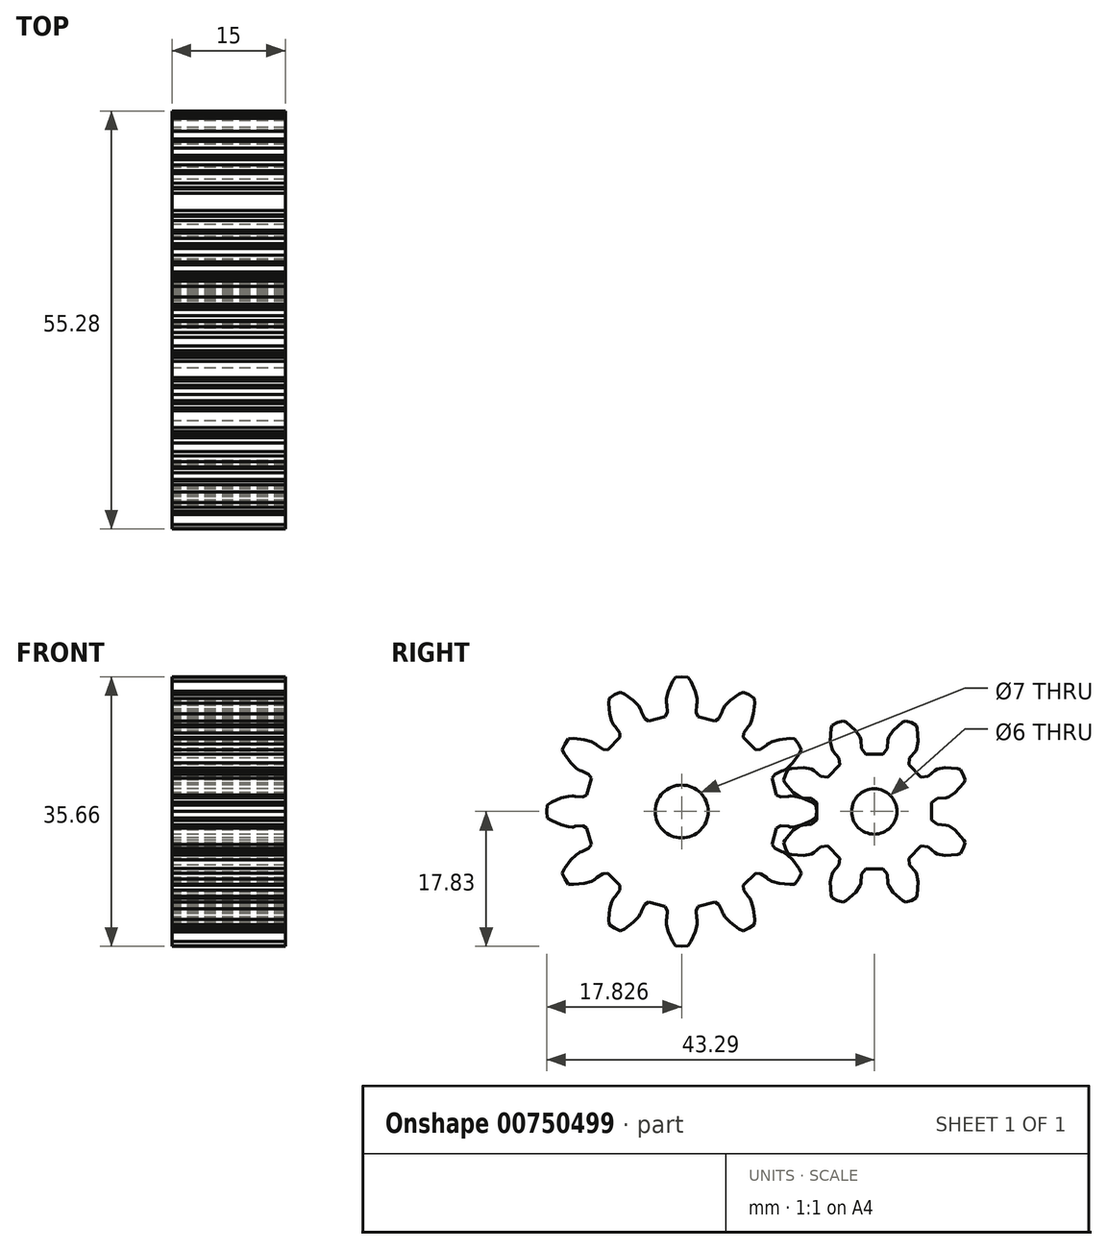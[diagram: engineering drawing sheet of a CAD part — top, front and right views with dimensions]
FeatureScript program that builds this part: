
annotation { "Feature Type Name" : "Feature", "Feature Type Description" : "" }
export const myFeature = defineFeature(function(context is Context, id is Id, definition is map)
    precondition{}
    {
        {
            var Q0;
            Q0=qCreatedBy(makeId("Right.planeOp"),FACE);
            var sketch = newSketch(context, id + "F0", { "sketchPlane" : qUnion([Q0])});
            skLineSegment(sketch, "E0", {"start": v(5.14, -9.6) * mm, "end": v(5.62, -8.91) * mm});
            skLineSegment(sketch, "E1", {"start": v(5.62, -8.91) * mm, "end": v(5.98, -8.15) * mm});
            skLineSegment(sketch, "E2", {"start": v(5.98, -8.15) * mm, "end": v(5.69, -7.55) * mm});
            skLineSegment(sketch, "E3", {"start": v(5.69, -7.55) * mm, "end": v(4.86, -6.4) * mm});
            skLineSegment(sketch, "E4", {"start": v(4.86, -6.4) * mm, "end": v(4.16, -5.74) * mm});
            skLineSegment(sketch, "E5", {"start": v(4.16, -5.74) * mm, "end": v(3.72, -5.44) * mm});
            skLineSegment(sketch, "E6", {"start": v(3.72, -5.44) * mm, "end": v(3.64, -5.4) * mm});
            skLineSegment(sketch, "E7", {"start": v(3.64, -5.4) * mm, "end": v(3.38, -5.34) * mm});
            skLineSegment(sketch, "E8", {"start": v(3.38, -5.34) * mm, "end": v(2.49, -4.9) * mm});
            skLineSegment(sketch, "E9", {"start": v(2.49, -4.9) * mm, "end": v(2.14, -4.38) * mm});
            skLineSegment(sketch, "E10", {"start": v(2.14, -4.38) * mm, "end": v(2.73, -2.18) * mm});
            skLineSegment(sketch, "E11", {"start": v(2.73, -2.18) * mm, "end": v(3.29, -1.91) * mm});
            skLineSegment(sketch, "E12", {"start": v(3.29, -1.91) * mm, "end": v(4.29, -1.97) * mm});
            skLineSegment(sketch, "E13", {"start": v(4.29, -1.97) * mm, "end": v(4.54, -2.04) * mm});
            skLineSegment(sketch, "E14", {"start": v(4.54, -2.04) * mm, "end": v(4.62, -2.05) * mm});
            skLineSegment(sketch, "E15", {"start": v(4.62, -2.05) * mm, "end": v(5.15, -2.02) * mm});
            skLineSegment(sketch, "E16", {"start": v(5.15, -2.02) * mm, "end": v(6.1, -1.79) * mm});
            skLineSegment(sketch, "E17", {"start": v(6.1, -1.79) * mm, "end": v(7.39, -1.21) * mm});
            skLineSegment(sketch, "E18", {"start": v(7.39, -1.21) * mm, "end": v(7.94, -0.84) * mm});
            skLineSegment(sketch, "E19", {"start": v(7.94, -0.84) * mm, "end": v(8.01, 0) * mm});
            skLineSegment(sketch, "E20", {"start": v(8.01, 0) * mm, "end": v(7.94, 0.84) * mm});
            skLineSegment(sketch, "E21", {"start": v(7.94, 0.84) * mm, "end": v(7.39, 1.21) * mm});
            skLineSegment(sketch, "E22", {"start": v(7.39, 1.21) * mm, "end": v(6.1, 1.79) * mm});
            skLineSegment(sketch, "E23", {"start": v(6.1, 1.79) * mm, "end": v(5.15, 2.02) * mm});
            skLineSegment(sketch, "E24", {"start": v(5.15, 2.02) * mm, "end": v(4.62, 2.05) * mm});
            skLineSegment(sketch, "E25", {"start": v(4.62, 2.05) * mm, "end": v(4.54, 2.04) * mm});
            skLineSegment(sketch, "E26", {"start": v(4.54, 2.04) * mm, "end": v(4.29, 1.97) * mm});
            skLineSegment(sketch, "E27", {"start": v(4.29, 1.97) * mm, "end": v(3.29, 1.91) * mm});
            skLineSegment(sketch, "E28", {"start": v(3.29, 1.91) * mm, "end": v(2.73, 2.18) * mm});
            skLineSegment(sketch, "E29", {"start": v(2.73, 2.18) * mm, "end": v(2.14, 4.38) * mm});
            skLineSegment(sketch, "E30", {"start": v(2.14, 4.38) * mm, "end": v(2.49, 4.9) * mm});
            skLineSegment(sketch, "E31", {"start": v(2.49, 4.9) * mm, "end": v(3.38, 5.34) * mm});
            skLineSegment(sketch, "E32", {"start": v(3.38, 5.34) * mm, "end": v(3.64, 5.4) * mm});
            skLineSegment(sketch, "E33", {"start": v(3.64, 5.4) * mm, "end": v(3.72, 5.44) * mm});
            skLineSegment(sketch, "E34", {"start": v(3.72, 5.44) * mm, "end": v(4.16, 5.74) * mm});
            skLineSegment(sketch, "E35", {"start": v(4.16, 5.74) * mm, "end": v(4.86, 6.4) * mm});
            skLineSegment(sketch, "E36", {"start": v(4.86, 6.4) * mm, "end": v(5.69, 7.55) * mm});
            skLineSegment(sketch, "E37", {"start": v(5.69, 7.55) * mm, "end": v(5.98, 8.15) * mm});
            skLineSegment(sketch, "E38", {"start": v(5.98, 8.15) * mm, "end": v(5.62, 8.91) * mm});
            skLineSegment(sketch, "E39", {"start": v(5.62, 8.91) * mm, "end": v(5.14, 9.6) * mm});
            skLineSegment(sketch, "E40", {"start": v(5.14, 9.6) * mm, "end": v(4.48, 9.65) * mm});
            skLineSegment(sketch, "E41", {"start": v(4.48, 9.65) * mm, "end": v(3.07, 9.5) * mm});
            skLineSegment(sketch, "E42", {"start": v(3.07, 9.5) * mm, "end": v(2.14, 9.23) * mm});
            skLineSegment(sketch, "E43", {"start": v(2.14, 9.23) * mm, "end": v(1.66, 9) * mm});
            skLineSegment(sketch, "E44", {"start": v(1.66, 9) * mm, "end": v(1.6, 8.95) * mm});
            skLineSegment(sketch, "E45", {"start": v(1.6, 8.95) * mm, "end": v(1.41, 8.76) * mm});
            skLineSegment(sketch, "E46", {"start": v(1.41, 8.76) * mm, "end": v(0.58, 8.2) * mm});
            skLineSegment(sketch, "E47", {"start": v(0.58, 8.2) * mm, "end": v(-0.04, 8.16) * mm});
            skLineSegment(sketch, "E48", {"start": v(-0.04, 8.16) * mm, "end": v(-1.65, 9.77) * mm});
            skLineSegment(sketch, "E49", {"start": v(-1.65, 9.77) * mm, "end": v(-1.6, 10.4) * mm});
            skLineSegment(sketch, "E50", {"start": v(-1.6, 10.4) * mm, "end": v(-1.06, 11.23) * mm});
            skLineSegment(sketch, "E51", {"start": v(-1.06, 11.23) * mm, "end": v(-0.87, 11.4) * mm});
            skLineSegment(sketch, "E52", {"start": v(-0.87, 11.4) * mm, "end": v(-0.82, 11.48) * mm});
            skLineSegment(sketch, "E53", {"start": v(-0.82, 11.48) * mm, "end": v(-0.58, 11.95) * mm});
            skLineSegment(sketch, "E54", {"start": v(-0.58, 11.95) * mm, "end": v(-0.31, 12.88) * mm});
            skLineSegment(sketch, "E55", {"start": v(-0.31, 12.88) * mm, "end": v(-0.16, 14.29) * mm});
            skLineSegment(sketch, "E56", {"start": v(-0.16, 14.29) * mm, "end": v(-0.2, 14.95) * mm});
            skLineSegment(sketch, "E57", {"start": v(-0.2, 14.95) * mm, "end": v(-0.9, 15.44) * mm});
            skLineSegment(sketch, "E58", {"start": v(-0.9, 15.44) * mm, "end": v(-1.67, 15.8) * mm});
            skLineSegment(sketch, "E59", {"start": v(-1.67, 15.8) * mm, "end": v(-2.26, 15.5) * mm});
            skLineSegment(sketch, "E60", {"start": v(-2.26, 15.5) * mm, "end": v(-3.4, 14.67) * mm});
            skLineSegment(sketch, "E61", {"start": v(-3.4, 14.67) * mm, "end": v(-4.08, 13.97) * mm});
            skLineSegment(sketch, "E62", {"start": v(-4.08, 13.97) * mm, "end": v(-4.37, 13.53) * mm});
            skLineSegment(sketch, "E63", {"start": v(-4.37, 13.53) * mm, "end": v(-4.41, 13.45) * mm});
            skLineSegment(sketch, "E64", {"start": v(-4.41, 13.45) * mm, "end": v(-4.47, 13.2) * mm});
            skLineSegment(sketch, "E65", {"start": v(-4.47, 13.2) * mm, "end": v(-4.92, 12.3) * mm});
            skLineSegment(sketch, "E66", {"start": v(-4.92, 12.3) * mm, "end": v(-5.43, 11.96) * mm});
            skLineSegment(sketch, "E67", {"start": v(-5.43, 11.96) * mm, "end": v(-7.63, 12.54) * mm});
            skLineSegment(sketch, "E68", {"start": v(-7.63, 12.54) * mm, "end": v(-7.9, 13.1) * mm});
            skLineSegment(sketch, "E69", {"start": v(-7.9, 13.1) * mm, "end": v(-7.84, 14.1) * mm});
            skLineSegment(sketch, "E70", {"start": v(-7.84, 14.1) * mm, "end": v(-7.77, 14.35) * mm});
            skLineSegment(sketch, "E71", {"start": v(-7.77, 14.35) * mm, "end": v(-7.76, 14.44) * mm});
            skLineSegment(sketch, "E72", {"start": v(-7.76, 14.44) * mm, "end": v(-7.8, 14.97) * mm});
            skLineSegment(sketch, "E73", {"start": v(-7.8, 14.97) * mm, "end": v(-8.03, 15.9) * mm});
            skLineSegment(sketch, "E74", {"start": v(-8.03, 15.9) * mm, "end": v(-8.6, 17.2) * mm});
            skLineSegment(sketch, "E75", {"start": v(-8.6, 17.2) * mm, "end": v(-8.97, 17.75) * mm});
            skLineSegment(sketch, "E76", {"start": v(-8.97, 17.75) * mm, "end": v(-9.81, 17.83) * mm});
            skLineSegment(sketch, "E77", {"start": v(-9.81, 17.83) * mm, "end": v(-10.66, 17.75) * mm});
            skLineSegment(sketch, "E78", {"start": v(-10.66, 17.75) * mm, "end": v(-11.03, 17.2) * mm});
            skLineSegment(sketch, "E79", {"start": v(-11.03, 17.2) * mm, "end": v(-11.6, 15.9) * mm});
            skLineSegment(sketch, "E80", {"start": v(-11.6, 15.9) * mm, "end": v(-11.83, 14.97) * mm});
            skLineSegment(sketch, "E81", {"start": v(-11.83, 14.97) * mm, "end": v(-11.87, 14.44) * mm});
            skLineSegment(sketch, "E82", {"start": v(-11.87, 14.44) * mm, "end": v(-11.86, 14.35) * mm});
            skLineSegment(sketch, "E83", {"start": v(-11.86, 14.35) * mm, "end": v(-11.79, 14.1) * mm});
            skLineSegment(sketch, "E84", {"start": v(-11.79, 14.1) * mm, "end": v(-11.73, 13.1) * mm});
            skLineSegment(sketch, "E85", {"start": v(-11.73, 13.1) * mm, "end": v(-12, 12.54) * mm});
            skLineSegment(sketch, "E86", {"start": v(-12, 12.54) * mm, "end": v(-14.2, 11.96) * mm});
            skLineSegment(sketch, "E87", {"start": v(-14.2, 11.96) * mm, "end": v(-14.71, 12.3) * mm});
            skLineSegment(sketch, "E88", {"start": v(-14.71, 12.3) * mm, "end": v(-15.16, 13.2) * mm});
            skLineSegment(sketch, "E89", {"start": v(-15.16, 13.2) * mm, "end": v(-15.22, 13.45) * mm});
            skLineSegment(sketch, "E90", {"start": v(-15.22, 13.45) * mm, "end": v(-15.25, 13.53) * mm});
            skLineSegment(sketch, "E91", {"start": v(-15.25, 13.53) * mm, "end": v(-15.55, 13.97) * mm});
            skLineSegment(sketch, "E92", {"start": v(-15.55, 13.97) * mm, "end": v(-16.22, 14.67) * mm});
            skLineSegment(sketch, "E93", {"start": v(-16.22, 14.67) * mm, "end": v(-17.36, 15.5) * mm});
            skLineSegment(sketch, "E94", {"start": v(-17.36, 15.5) * mm, "end": v(-17.96, 15.8) * mm});
            skLineSegment(sketch, "E95", {"start": v(-17.96, 15.8) * mm, "end": v(-18.73, 15.44) * mm});
            skLineSegment(sketch, "E96", {"start": v(-18.73, 15.44) * mm, "end": v(-19.42, 14.95) * mm});
            skLineSegment(sketch, "E97", {"start": v(-19.42, 14.95) * mm, "end": v(-19.47, 14.29) * mm});
            skLineSegment(sketch, "E98", {"start": v(-19.47, 14.29) * mm, "end": v(-19.32, 12.88) * mm});
            skLineSegment(sketch, "E99", {"start": v(-19.32, 12.88) * mm, "end": v(-19.05, 11.95) * mm});
            skLineSegment(sketch, "E100", {"start": v(-19.05, 11.95) * mm, "end": v(-18.81, 11.48) * mm});
            skLineSegment(sketch, "E101", {"start": v(-18.81, 11.48) * mm, "end": v(-18.76, 11.4) * mm});
            skLineSegment(sketch, "E102", {"start": v(-18.76, 11.4) * mm, "end": v(-18.57, 11.23) * mm});
            skLineSegment(sketch, "E103", {"start": v(-18.57, 11.23) * mm, "end": v(-18.02, 10.4) * mm});
            skLineSegment(sketch, "E104", {"start": v(-18.02, 10.4) * mm, "end": v(-17.98, 9.77) * mm});
            skLineSegment(sketch, "E105", {"start": v(-17.98, 9.77) * mm, "end": v(-19.59, 8.16) * mm});
            skLineSegment(sketch, "E106", {"start": v(-19.59, 8.16) * mm, "end": v(-20.2, 8.2) * mm});
            skLineSegment(sketch, "E107", {"start": v(-20.2, 8.2) * mm, "end": v(-21.04, 8.76) * mm});
            skLineSegment(sketch, "E108", {"start": v(-21.04, 8.76) * mm, "end": v(-21.22, 8.95) * mm});
            skLineSegment(sketch, "E109", {"start": v(-21.22, 8.95) * mm, "end": v(-21.3, 9) * mm});
            skLineSegment(sketch, "E110", {"start": v(-21.3, 9) * mm, "end": v(-21.77, 9.23) * mm});
            skLineSegment(sketch, "E111", {"start": v(-21.77, 9.23) * mm, "end": v(-22.7, 9.5) * mm});
            skLineSegment(sketch, "E112", {"start": v(-22.7, 9.5) * mm, "end": v(-24.1, 9.65) * mm});
            skLineSegment(sketch, "E113", {"start": v(-24.1, 9.65) * mm, "end": v(-24.77, 9.6) * mm});
            skLineSegment(sketch, "E114", {"start": v(-24.77, 9.6) * mm, "end": v(-25.25, 8.91) * mm});
            skLineSegment(sketch, "E115", {"start": v(-25.25, 8.91) * mm, "end": v(-25.6, 8.15) * mm});
            skLineSegment(sketch, "E116", {"start": v(-25.6, 8.15) * mm, "end": v(-25.32, 7.55) * mm});
            skLineSegment(sketch, "E117", {"start": v(-25.32, 7.55) * mm, "end": v(-24.48, 6.4) * mm});
            skLineSegment(sketch, "E118", {"start": v(-24.48, 6.4) * mm, "end": v(-23.78, 5.74) * mm});
            skLineSegment(sketch, "E119", {"start": v(-23.78, 5.74) * mm, "end": v(-23.34, 5.44) * mm});
            skLineSegment(sketch, "E120", {"start": v(-23.34, 5.44) * mm, "end": v(-23.26, 5.4) * mm});
            skLineSegment(sketch, "E121", {"start": v(-23.26, 5.4) * mm, "end": v(-23.01, 5.34) * mm});
            skLineSegment(sketch, "E122", {"start": v(-23.01, 5.34) * mm, "end": v(-22.12, 4.9) * mm});
            skLineSegment(sketch, "E123", {"start": v(-22.12, 4.9) * mm, "end": v(-21.77, 4.38) * mm});
            skLineSegment(sketch, "E124", {"start": v(-21.77, 4.38) * mm, "end": v(-22.36, 2.18) * mm});
            skLineSegment(sketch, "E125", {"start": v(-22.36, 2.18) * mm, "end": v(-22.92, 1.91) * mm});
            skLineSegment(sketch, "E126", {"start": v(-22.92, 1.91) * mm, "end": v(-23.92, 1.97) * mm});
            skLineSegment(sketch, "E127", {"start": v(-23.92, 1.97) * mm, "end": v(-24.16, 2.04) * mm});
            skLineSegment(sketch, "E128", {"start": v(-24.16, 2.04) * mm, "end": v(-24.25, 2.05) * mm});
            skLineSegment(sketch, "E129", {"start": v(-24.25, 2.05) * mm, "end": v(-24.78, 2.02) * mm});
            skLineSegment(sketch, "E130", {"start": v(-24.78, 2.02) * mm, "end": v(-25.72, 1.79) * mm});
            skLineSegment(sketch, "E131", {"start": v(-25.72, 1.79) * mm, "end": v(-27.02, 1.21) * mm});
            skLineSegment(sketch, "E132", {"start": v(-27.02, 1.21) * mm, "end": v(-27.57, 0.84) * mm});
            skLineSegment(sketch, "E133", {"start": v(-27.57, 0.84) * mm, "end": v(-27.64, 0) * mm});
            skLineSegment(sketch, "E134", {"start": v(-27.64, 0) * mm, "end": v(-27.57, -0.84) * mm});
            skLineSegment(sketch, "E135", {"start": v(-27.57, -0.84) * mm, "end": v(-27.02, -1.21) * mm});
            skLineSegment(sketch, "E136", {"start": v(-27.02, -1.21) * mm, "end": v(-25.72, -1.79) * mm});
            skLineSegment(sketch, "E137", {"start": v(-25.72, -1.79) * mm, "end": v(-24.78, -2.02) * mm});
            skLineSegment(sketch, "E138", {"start": v(-24.78, -2.02) * mm, "end": v(-24.25, -2.05) * mm});
            skLineSegment(sketch, "E139", {"start": v(-24.25, -2.05) * mm, "end": v(-24.16, -2.04) * mm});
            skLineSegment(sketch, "E140", {"start": v(-24.16, -2.04) * mm, "end": v(-23.92, -1.97) * mm});
            skLineSegment(sketch, "E141", {"start": v(-23.92, -1.97) * mm, "end": v(-22.92, -1.91) * mm});
            skLineSegment(sketch, "E142", {"start": v(-22.92, -1.91) * mm, "end": v(-22.36, -2.18) * mm});
            skLineSegment(sketch, "E143", {"start": v(-22.36, -2.18) * mm, "end": v(-21.77, -4.38) * mm});
            skLineSegment(sketch, "E144", {"start": v(-21.77, -4.38) * mm, "end": v(-22.12, -4.9) * mm});
            skLineSegment(sketch, "E145", {"start": v(-22.12, -4.9) * mm, "end": v(-23.01, -5.34) * mm});
            skLineSegment(sketch, "E146", {"start": v(-23.01, -5.34) * mm, "end": v(-23.26, -5.4) * mm});
            skLineSegment(sketch, "E147", {"start": v(-23.26, -5.4) * mm, "end": v(-23.34, -5.44) * mm});
            skLineSegment(sketch, "E148", {"start": v(-23.34, -5.44) * mm, "end": v(-23.78, -5.74) * mm});
            skLineSegment(sketch, "E149", {"start": v(-23.78, -5.74) * mm, "end": v(-24.48, -6.4) * mm});
            skLineSegment(sketch, "E150", {"start": v(-24.48, -6.4) * mm, "end": v(-25.32, -7.55) * mm});
            skLineSegment(sketch, "E151", {"start": v(-25.32, -7.55) * mm, "end": v(-25.6, -8.15) * mm});
            skLineSegment(sketch, "E152", {"start": v(-25.6, -8.15) * mm, "end": v(-25.25, -8.91) * mm});
            skLineSegment(sketch, "E153", {"start": v(-25.25, -8.91) * mm, "end": v(-24.77, -9.6) * mm});
            skLineSegment(sketch, "E154", {"start": v(-24.77, -9.6) * mm, "end": v(-24.1, -9.65) * mm});
            skLineSegment(sketch, "E155", {"start": v(-24.1, -9.65) * mm, "end": v(-22.7, -9.5) * mm});
            skLineSegment(sketch, "E156", {"start": v(-22.7, -9.5) * mm, "end": v(-21.77, -9.23) * mm});
            skLineSegment(sketch, "E157", {"start": v(-21.77, -9.23) * mm, "end": v(-21.3, -9) * mm});
            skLineSegment(sketch, "E158", {"start": v(-21.3, -9) * mm, "end": v(-21.22, -8.95) * mm});
            skLineSegment(sketch, "E159", {"start": v(-21.22, -8.95) * mm, "end": v(-21.04, -8.76) * mm});
            skLineSegment(sketch, "E160", {"start": v(-21.04, -8.76) * mm, "end": v(-20.2, -8.2) * mm});
            skLineSegment(sketch, "E161", {"start": v(-20.2, -8.2) * mm, "end": v(-19.59, -8.16) * mm});
            skLineSegment(sketch, "E162", {"start": v(-19.59, -8.16) * mm, "end": v(-17.98, -9.77) * mm});
            skLineSegment(sketch, "E163", {"start": v(-17.98, -9.77) * mm, "end": v(-18.02, -10.4) * mm});
            skLineSegment(sketch, "E164", {"start": v(-18.02, -10.4) * mm, "end": v(-18.57, -11.23) * mm});
            skLineSegment(sketch, "E165", {"start": v(-18.57, -11.23) * mm, "end": v(-18.76, -11.4) * mm});
            skLineSegment(sketch, "E166", {"start": v(-18.76, -11.4) * mm, "end": v(-18.81, -11.48) * mm});
            skLineSegment(sketch, "E167", {"start": v(-18.81, -11.48) * mm, "end": v(-19.05, -11.95) * mm});
            skLineSegment(sketch, "E168", {"start": v(-19.05, -11.95) * mm, "end": v(-19.32, -12.88) * mm});
            skLineSegment(sketch, "E169", {"start": v(-19.32, -12.88) * mm, "end": v(-19.47, -14.29) * mm});
            skLineSegment(sketch, "E170", {"start": v(-19.47, -14.29) * mm, "end": v(-19.42, -14.95) * mm});
            skLineSegment(sketch, "E171", {"start": v(-19.42, -14.95) * mm, "end": v(-18.73, -15.44) * mm});
            skLineSegment(sketch, "E172", {"start": v(-18.73, -15.44) * mm, "end": v(-17.96, -15.8) * mm});
            skLineSegment(sketch, "E173", {"start": v(-17.96, -15.8) * mm, "end": v(-17.36, -15.5) * mm});
            skLineSegment(sketch, "E174", {"start": v(-17.36, -15.5) * mm, "end": v(-16.22, -14.67) * mm});
            skLineSegment(sketch, "E175", {"start": v(-16.22, -14.67) * mm, "end": v(-15.55, -13.97) * mm});
            skLineSegment(sketch, "E176", {"start": v(-15.55, -13.97) * mm, "end": v(-15.25, -13.53) * mm});
            skLineSegment(sketch, "E177", {"start": v(-15.25, -13.53) * mm, "end": v(-15.22, -13.45) * mm});
            skLineSegment(sketch, "E178", {"start": v(-15.22, -13.45) * mm, "end": v(-15.16, -13.2) * mm});
            skLineSegment(sketch, "E179", {"start": v(-15.16, -13.2) * mm, "end": v(-14.71, -12.3) * mm});
            skLineSegment(sketch, "E180", {"start": v(-14.71, -12.3) * mm, "end": v(-14.2, -11.96) * mm});
            skLineSegment(sketch, "E181", {"start": v(-14.2, -11.96) * mm, "end": v(-12, -12.54) * mm});
            skLineSegment(sketch, "E182", {"start": v(-12, -12.54) * mm, "end": v(-11.73, -13.1) * mm});
            skLineSegment(sketch, "E183", {"start": v(-11.73, -13.1) * mm, "end": v(-11.79, -14.1) * mm});
            skLineSegment(sketch, "E184", {"start": v(-11.79, -14.1) * mm, "end": v(-11.86, -14.35) * mm});
            skLineSegment(sketch, "E185", {"start": v(-11.86, -14.35) * mm, "end": v(-11.87, -14.44) * mm});
            skLineSegment(sketch, "E186", {"start": v(-11.87, -14.44) * mm, "end": v(-11.83, -14.97) * mm});
            skLineSegment(sketch, "E187", {"start": v(-11.83, -14.97) * mm, "end": v(-11.6, -15.9) * mm});
            skLineSegment(sketch, "E188", {"start": v(-11.6, -15.9) * mm, "end": v(-11.03, -17.2) * mm});
            skLineSegment(sketch, "E189", {"start": v(-11.03, -17.2) * mm, "end": v(-10.66, -17.75) * mm});
            skLineSegment(sketch, "E190", {"start": v(-10.66, -17.75) * mm, "end": v(-9.81, -17.83) * mm});
            skLineSegment(sketch, "E191", {"start": v(-9.81, -17.83) * mm, "end": v(-8.97, -17.75) * mm});
            skLineSegment(sketch, "E192", {"start": v(-8.97, -17.75) * mm, "end": v(-8.6, -17.2) * mm});
            skLineSegment(sketch, "E193", {"start": v(-8.6, -17.2) * mm, "end": v(-8.03, -15.9) * mm});
            skLineSegment(sketch, "E194", {"start": v(-8.03, -15.9) * mm, "end": v(-7.8, -14.97) * mm});
            skLineSegment(sketch, "E195", {"start": v(-7.8, -14.97) * mm, "end": v(-7.76, -14.44) * mm});
            skLineSegment(sketch, "E196", {"start": v(-7.76, -14.44) * mm, "end": v(-7.77, -14.35) * mm});
            skLineSegment(sketch, "E197", {"start": v(-7.77, -14.35) * mm, "end": v(-7.84, -14.1) * mm});
            skLineSegment(sketch, "E198", {"start": v(-7.84, -14.1) * mm, "end": v(-7.9, -13.1) * mm});
            skLineSegment(sketch, "E199", {"start": v(-7.9, -13.1) * mm, "end": v(-7.63, -12.54) * mm});
            skLineSegment(sketch, "E200", {"start": v(-7.63, -12.54) * mm, "end": v(-5.43, -11.96) * mm});
            skLineSegment(sketch, "E201", {"start": v(-5.43, -11.96) * mm, "end": v(-4.92, -12.3) * mm});
            skLineSegment(sketch, "E202", {"start": v(-4.92, -12.3) * mm, "end": v(-4.47, -13.2) * mm});
            skLineSegment(sketch, "E203", {"start": v(-4.47, -13.2) * mm, "end": v(-4.41, -13.45) * mm});
            skLineSegment(sketch, "E204", {"start": v(-4.41, -13.45) * mm, "end": v(-4.37, -13.53) * mm});
            skLineSegment(sketch, "E205", {"start": v(-4.37, -13.53) * mm, "end": v(-4.08, -13.97) * mm});
            skLineSegment(sketch, "E206", {"start": v(-4.08, -13.97) * mm, "end": v(-3.4, -14.67) * mm});
            skLineSegment(sketch, "E207", {"start": v(-3.4, -14.67) * mm, "end": v(-2.26, -15.5) * mm});
            skLineSegment(sketch, "E208", {"start": v(-2.26, -15.5) * mm, "end": v(-1.67, -15.8) * mm});
            skLineSegment(sketch, "E209", {"start": v(-1.67, -15.8) * mm, "end": v(-0.9, -15.44) * mm});
            skLineSegment(sketch, "E210", {"start": v(-0.9, -15.44) * mm, "end": v(-0.2, -14.95) * mm});
            skLineSegment(sketch, "E211", {"start": v(-0.2, -14.95) * mm, "end": v(-0.16, -14.29) * mm});
            skLineSegment(sketch, "E212", {"start": v(-0.16, -14.29) * mm, "end": v(-0.31, -12.88) * mm});
            skLineSegment(sketch, "E213", {"start": v(-0.31, -12.88) * mm, "end": v(-0.58, -11.95) * mm});
            skLineSegment(sketch, "E214", {"start": v(-0.58, -11.95) * mm, "end": v(-0.82, -11.48) * mm});
            skLineSegment(sketch, "E215", {"start": v(-0.82, -11.48) * mm, "end": v(-0.87, -11.4) * mm});
            skLineSegment(sketch, "E216", {"start": v(-0.87, -11.4) * mm, "end": v(-1.06, -11.23) * mm});
            skLineSegment(sketch, "E217", {"start": v(-1.06, -11.23) * mm, "end": v(-1.6, -10.4) * mm});
            skLineSegment(sketch, "E218", {"start": v(-1.6, -10.4) * mm, "end": v(-1.65, -9.77) * mm});
            skLineSegment(sketch, "E219", {"start": v(-1.65, -9.77) * mm, "end": v(-0.04, -8.16) * mm});
            skLineSegment(sketch, "E220", {"start": v(-0.04, -8.16) * mm, "end": v(0.58, -8.2) * mm});
            skLineSegment(sketch, "E221", {"start": v(0.58, -8.2) * mm, "end": v(1.41, -8.76) * mm});
            skLineSegment(sketch, "E222", {"start": v(1.41, -8.76) * mm, "end": v(1.6, -8.95) * mm});
            skLineSegment(sketch, "E223", {"start": v(1.6, -8.95) * mm, "end": v(1.66, -9) * mm});
            skLineSegment(sketch, "E224", {"start": v(1.66, -9) * mm, "end": v(2.14, -9.23) * mm});
            skLineSegment(sketch, "E225", {"start": v(2.14, -9.23) * mm, "end": v(3.07, -9.5) * mm});
            skLineSegment(sketch, "E226", {"start": v(3.07, -9.5) * mm, "end": v(4.48, -9.65) * mm});
            skLineSegment(sketch, "E227", {"start": v(4.48, -9.65) * mm, "end": v(5.14, -9.6) * mm});
            skLineSegment(sketch, "E228", {"start": v(-9.4, -1.96) * mm, "end": v(-9.81, -2) * mm});
            skLineSegment(sketch, "E229", {"start": v(-9.81, -2) * mm, "end": v(-10.23, -1.96) * mm});
            skLineSegment(sketch, "E230", {"start": v(-10.23, -1.96) * mm, "end": v(-10.63, -1.83) * mm});
            skLineSegment(sketch, "E231", {"start": v(-10.63, -1.83) * mm, "end": v(-10.99, -1.62) * mm});
            skLineSegment(sketch, "E232", {"start": v(-10.99, -1.62) * mm, "end": v(-11.3, -1.34) * mm});
            skLineSegment(sketch, "E233", {"start": v(-11.3, -1.34) * mm, "end": v(-11.55, -1) * mm});
            skLineSegment(sketch, "E234", {"start": v(-11.55, -1) * mm, "end": v(-11.72, -0.62) * mm});
            skLineSegment(sketch, "E235", {"start": v(-11.72, -0.62) * mm, "end": v(-11.8, -0.2) * mm});
            skLineSegment(sketch, "E236", {"start": v(-11.8, -0.2) * mm, "end": v(-11.8, 0.2) * mm});
            skLineSegment(sketch, "E237", {"start": v(-11.8, 0.2) * mm, "end": v(-11.72, 0.62) * mm});
            skLineSegment(sketch, "E238", {"start": v(-11.72, 0.62) * mm, "end": v(-11.55, 1) * mm});
            skLineSegment(sketch, "E239", {"start": v(-11.55, 1) * mm, "end": v(-11.3, 1.34) * mm});
            skLineSegment(sketch, "E240", {"start": v(-11.3, 1.34) * mm, "end": v(-10.99, 1.62) * mm});
            skLineSegment(sketch, "E241", {"start": v(-10.99, 1.62) * mm, "end": v(-10.63, 1.83) * mm});
            skLineSegment(sketch, "E242", {"start": v(-10.63, 1.83) * mm, "end": v(-10.23, 1.96) * mm});
            skLineSegment(sketch, "E243", {"start": v(-10.23, 1.96) * mm, "end": v(-9.81, 2) * mm});
            skLineSegment(sketch, "E244", {"start": v(-9.81, 2) * mm, "end": v(-9.4, 1.96) * mm});
            skLineSegment(sketch, "E245", {"start": v(-9.4, 1.96) * mm, "end": v(-9, 1.83) * mm});
            skLineSegment(sketch, "E246", {"start": v(-9, 1.83) * mm, "end": v(-8.64, 1.62) * mm});
            skLineSegment(sketch, "E247", {"start": v(-8.64, 1.62) * mm, "end": v(-8.33, 1.34) * mm});
            skLineSegment(sketch, "E248", {"start": v(-8.33, 1.34) * mm, "end": v(-8.08, 1) * mm});
            skLineSegment(sketch, "E249", {"start": v(-8.08, 1) * mm, "end": v(-7.91, 0.62) * mm});
            skLineSegment(sketch, "E250", {"start": v(-7.91, 0.62) * mm, "end": v(-7.83, 0.2) * mm});
            skLineSegment(sketch, "E251", {"start": v(-7.83, 0.2) * mm, "end": v(-7.83, -0.2) * mm});
            skLineSegment(sketch, "E252", {"start": v(-7.83, -0.2) * mm, "end": v(-7.91, -0.62) * mm});
            skLineSegment(sketch, "E253", {"start": v(-7.91, -0.62) * mm, "end": v(-8.08, -1) * mm});
            skLineSegment(sketch, "E254", {"start": v(-8.08, -1) * mm, "end": v(-8.33, -1.34) * mm});
            skLineSegment(sketch, "E255", {"start": v(-8.33, -1.34) * mm, "end": v(-8.64, -1.62) * mm});
            skLineSegment(sketch, "E256", {"start": v(-8.64, -1.62) * mm, "end": v(-9, -1.83) * mm});
            skLineSegment(sketch, "E257", {"start": v(-9, -1.83) * mm, "end": v(-9.4, -1.96) * mm});
            skLineSegment(sketch, "E258", {"start": v(4.25, 5.56) * mm, "end": v(3.89, 4.87) * mm});
            skLineSegment(sketch, "E259", {"start": v(3.89, 4.87) * mm, "end": v(3.66, 4.13) * mm});
            skLineSegment(sketch, "E260", {"start": v(3.66, 4.13) * mm, "end": v(3.84, 3.76) * mm});
            skLineSegment(sketch, "E261", {"start": v(3.84, 3.76) * mm, "end": v(4.96, 2.48) * mm});
            skLineSegment(sketch, "E262", {"start": v(4.96, 2.48) * mm, "end": v(5.8, 1.9) * mm});
            skLineSegment(sketch, "E263", {"start": v(5.8, 1.9) * mm, "end": v(6.15, 1.8) * mm});
            skLineSegment(sketch, "E264", {"start": v(6.15, 1.8) * mm, "end": v(7.33, 1.71) * mm});
            skLineSegment(sketch, "E265", {"start": v(7.33, 1.71) * mm, "end": v(8.06, 1.14) * mm});
            skLineSegment(sketch, "E266", {"start": v(8.06, 1.14) * mm, "end": v(8.06, -1.14) * mm});
            skLineSegment(sketch, "E267", {"start": v(8.06, -1.14) * mm, "end": v(7.33, -1.71) * mm});
            skLineSegment(sketch, "E268", {"start": v(7.33, -1.71) * mm, "end": v(6.15, -1.8) * mm});
            skLineSegment(sketch, "E269", {"start": v(6.15, -1.8) * mm, "end": v(5.8, -1.9) * mm});
            skLineSegment(sketch, "E270", {"start": v(5.8, -1.9) * mm, "end": v(4.96, -2.48) * mm});
            skLineSegment(sketch, "E271", {"start": v(4.96, -2.48) * mm, "end": v(3.84, -3.76) * mm});
            skLineSegment(sketch, "E272", {"start": v(3.84, -3.76) * mm, "end": v(3.66, -4.13) * mm});
            skLineSegment(sketch, "E273", {"start": v(3.66, -4.13) * mm, "end": v(3.89, -4.87) * mm});
            skLineSegment(sketch, "E274", {"start": v(3.89, -4.87) * mm, "end": v(4.25, -5.56) * mm});
            skLineSegment(sketch, "E275", {"start": v(4.25, -5.56) * mm, "end": v(4.65, -5.7) * mm});
            skLineSegment(sketch, "E276", {"start": v(4.65, -5.7) * mm, "end": v(6.33, -5.8) * mm});
            skLineSegment(sketch, "E277", {"start": v(6.33, -5.8) * mm, "end": v(7.34, -5.6) * mm});
            skLineSegment(sketch, "E278", {"start": v(7.34, -5.6) * mm, "end": v(7.67, -5.45) * mm});
            skLineSegment(sketch, "E279", {"start": v(7.67, -5.45) * mm, "end": v(8.56, -4.67) * mm});
            skLineSegment(sketch, "E280", {"start": v(8.56, -4.67) * mm, "end": v(9.48, -4.56) * mm});
            skLineSegment(sketch, "E281", {"start": v(9.48, -4.56) * mm, "end": v(11.09, -6.17) * mm});
            skLineSegment(sketch, "E282", {"start": v(11.09, -6.17) * mm, "end": v(10.98, -7.1) * mm});
            skLineSegment(sketch, "E283", {"start": v(10.98, -7.1) * mm, "end": v(10.2, -7.98) * mm});
            skLineSegment(sketch, "E284", {"start": v(10.2, -7.98) * mm, "end": v(10.04, -8.3) * mm});
            skLineSegment(sketch, "E285", {"start": v(10.04, -8.3) * mm, "end": v(9.84, -9.32) * mm});
            skLineSegment(sketch, "E286", {"start": v(9.84, -9.32) * mm, "end": v(9.96, -11) * mm});
            skLineSegment(sketch, "E287", {"start": v(9.96, -11) * mm, "end": v(10.1, -11.4) * mm});
            skLineSegment(sketch, "E288", {"start": v(10.1, -11.4) * mm, "end": v(10.78, -11.76) * mm});
            skLineSegment(sketch, "E289", {"start": v(10.78, -11.76) * mm, "end": v(11.52, -11.99) * mm});
            skLineSegment(sketch, "E290", {"start": v(11.52, -11.99) * mm, "end": v(11.9, -11.8) * mm});
            skLineSegment(sketch, "E291", {"start": v(11.9, -11.8) * mm, "end": v(13.17, -10.7) * mm});
            skLineSegment(sketch, "E292", {"start": v(13.17, -10.7) * mm, "end": v(13.74, -9.84) * mm});
            skLineSegment(sketch, "E293", {"start": v(13.74, -9.84) * mm, "end": v(13.86, -9.5) * mm});
            skLineSegment(sketch, "E294", {"start": v(13.86, -9.5) * mm, "end": v(13.94, -8.32) * mm});
            skLineSegment(sketch, "E295", {"start": v(13.94, -8.32) * mm, "end": v(14.51, -7.59) * mm});
            skLineSegment(sketch, "E296", {"start": v(14.51, -7.59) * mm, "end": v(16.79, -7.59) * mm});
            skLineSegment(sketch, "E297", {"start": v(16.79, -7.59) * mm, "end": v(17.36, -8.32) * mm});
            skLineSegment(sketch, "E298", {"start": v(17.36, -8.32) * mm, "end": v(17.44, -9.5) * mm});
            skLineSegment(sketch, "E299", {"start": v(17.44, -9.5) * mm, "end": v(17.56, -9.84) * mm});
            skLineSegment(sketch, "E300", {"start": v(17.56, -9.84) * mm, "end": v(18.13, -10.7) * mm});
            skLineSegment(sketch, "E301", {"start": v(18.13, -10.7) * mm, "end": v(19.4, -11.8) * mm});
            skLineSegment(sketch, "E302", {"start": v(19.4, -11.8) * mm, "end": v(19.78, -11.99) * mm});
            skLineSegment(sketch, "E303", {"start": v(19.78, -11.99) * mm, "end": v(20.52, -11.76) * mm});
            skLineSegment(sketch, "E304", {"start": v(20.52, -11.76) * mm, "end": v(21.2, -11.4) * mm});
            skLineSegment(sketch, "E305", {"start": v(21.2, -11.4) * mm, "end": v(21.34, -11) * mm});
            skLineSegment(sketch, "E306", {"start": v(21.34, -11) * mm, "end": v(21.46, -9.32) * mm});
            skLineSegment(sketch, "E307", {"start": v(21.46, -9.32) * mm, "end": v(21.26, -8.3) * mm});
            skLineSegment(sketch, "E308", {"start": v(21.26, -8.3) * mm, "end": v(21.1, -7.98) * mm});
            skLineSegment(sketch, "E309", {"start": v(21.1, -7.98) * mm, "end": v(20.32, -7.1) * mm});
            skLineSegment(sketch, "E310", {"start": v(20.32, -7.1) * mm, "end": v(20.21, -6.17) * mm});
            skLineSegment(sketch, "E311", {"start": v(20.21, -6.17) * mm, "end": v(21.82, -4.56) * mm});
            skLineSegment(sketch, "E312", {"start": v(21.82, -4.56) * mm, "end": v(22.74, -4.67) * mm});
            skLineSegment(sketch, "E313", {"start": v(22.74, -4.67) * mm, "end": v(23.63, -5.45) * mm});
            skLineSegment(sketch, "E314", {"start": v(23.63, -5.45) * mm, "end": v(23.96, -5.6) * mm});
            skLineSegment(sketch, "E315", {"start": v(23.96, -5.6) * mm, "end": v(24.97, -5.8) * mm});
            skLineSegment(sketch, "E316", {"start": v(24.97, -5.8) * mm, "end": v(26.66, -5.7) * mm});
            skLineSegment(sketch, "E317", {"start": v(26.66, -5.7) * mm, "end": v(27.05, -5.56) * mm});
            skLineSegment(sketch, "E318", {"start": v(27.05, -5.56) * mm, "end": v(27.41, -4.87) * mm});
            skLineSegment(sketch, "E319", {"start": v(27.41, -4.87) * mm, "end": v(27.64, -4.13) * mm});
            skLineSegment(sketch, "E320", {"start": v(27.64, -4.13) * mm, "end": v(27.46, -3.76) * mm});
            skLineSegment(sketch, "E321", {"start": v(27.46, -3.76) * mm, "end": v(26.35, -2.48) * mm});
            skLineSegment(sketch, "E322", {"start": v(26.35, -2.48) * mm, "end": v(25.5, -1.9) * mm});
            skLineSegment(sketch, "E323", {"start": v(25.5, -1.9) * mm, "end": v(25.15, -1.8) * mm});
            skLineSegment(sketch, "E324", {"start": v(25.15, -1.8) * mm, "end": v(23.97, -1.71) * mm});
            skLineSegment(sketch, "E325", {"start": v(23.97, -1.71) * mm, "end": v(23.24, -1.14) * mm});
            skLineSegment(sketch, "E326", {"start": v(23.24, -1.14) * mm, "end": v(23.24, 1.14) * mm});
            skLineSegment(sketch, "E327", {"start": v(23.24, 1.14) * mm, "end": v(23.97, 1.71) * mm});
            skLineSegment(sketch, "E328", {"start": v(23.97, 1.71) * mm, "end": v(25.15, 1.8) * mm});
            skLineSegment(sketch, "E329", {"start": v(25.15, 1.8) * mm, "end": v(25.5, 1.9) * mm});
            skLineSegment(sketch, "E330", {"start": v(25.5, 1.9) * mm, "end": v(26.35, 2.48) * mm});
            skLineSegment(sketch, "E331", {"start": v(26.35, 2.48) * mm, "end": v(27.46, 3.76) * mm});
            skLineSegment(sketch, "E332", {"start": v(27.46, 3.76) * mm, "end": v(27.64, 4.13) * mm});
            skLineSegment(sketch, "E333", {"start": v(27.64, 4.13) * mm, "end": v(27.41, 4.87) * mm});
            skLineSegment(sketch, "E334", {"start": v(27.41, 4.87) * mm, "end": v(27.05, 5.56) * mm});
            skLineSegment(sketch, "E335", {"start": v(27.05, 5.56) * mm, "end": v(26.66, 5.7) * mm});
            skLineSegment(sketch, "E336", {"start": v(26.66, 5.7) * mm, "end": v(24.97, 5.8) * mm});
            skLineSegment(sketch, "E337", {"start": v(24.97, 5.8) * mm, "end": v(23.96, 5.6) * mm});
            skLineSegment(sketch, "E338", {"start": v(23.96, 5.6) * mm, "end": v(23.63, 5.45) * mm});
            skLineSegment(sketch, "E339", {"start": v(23.63, 5.45) * mm, "end": v(22.74, 4.67) * mm});
            skLineSegment(sketch, "E340", {"start": v(22.74, 4.67) * mm, "end": v(21.82, 4.56) * mm});
            skLineSegment(sketch, "E341", {"start": v(21.82, 4.56) * mm, "end": v(20.21, 6.17) * mm});
            skLineSegment(sketch, "E342", {"start": v(20.21, 6.17) * mm, "end": v(20.32, 7.1) * mm});
            skLineSegment(sketch, "E343", {"start": v(20.32, 7.1) * mm, "end": v(21.1, 7.98) * mm});
            skLineSegment(sketch, "E344", {"start": v(21.1, 7.98) * mm, "end": v(21.26, 8.3) * mm});
            skLineSegment(sketch, "E345", {"start": v(21.26, 8.3) * mm, "end": v(21.46, 9.32) * mm});
            skLineSegment(sketch, "E346", {"start": v(21.46, 9.32) * mm, "end": v(21.34, 11) * mm});
            skLineSegment(sketch, "E347", {"start": v(21.34, 11) * mm, "end": v(21.2, 11.4) * mm});
            skLineSegment(sketch, "E348", {"start": v(21.2, 11.4) * mm, "end": v(20.52, 11.76) * mm});
            skLineSegment(sketch, "E349", {"start": v(20.52, 11.76) * mm, "end": v(19.78, 11.99) * mm});
            skLineSegment(sketch, "E350", {"start": v(19.78, 11.99) * mm, "end": v(19.4, 11.8) * mm});
            skLineSegment(sketch, "E351", {"start": v(19.4, 11.8) * mm, "end": v(18.13, 10.7) * mm});
            skLineSegment(sketch, "E352", {"start": v(18.13, 10.7) * mm, "end": v(17.56, 9.84) * mm});
            skLineSegment(sketch, "E353", {"start": v(17.56, 9.84) * mm, "end": v(17.44, 9.5) * mm});
            skLineSegment(sketch, "E354", {"start": v(17.44, 9.5) * mm, "end": v(17.36, 8.32) * mm});
            skLineSegment(sketch, "E355", {"start": v(17.36, 8.32) * mm, "end": v(16.79, 7.59) * mm});
            skLineSegment(sketch, "E356", {"start": v(16.79, 7.59) * mm, "end": v(14.51, 7.59) * mm});
            skLineSegment(sketch, "E357", {"start": v(14.51, 7.59) * mm, "end": v(13.94, 8.32) * mm});
            skLineSegment(sketch, "E358", {"start": v(13.94, 8.32) * mm, "end": v(13.86, 9.5) * mm});
            skLineSegment(sketch, "E359", {"start": v(13.86, 9.5) * mm, "end": v(13.74, 9.84) * mm});
            skLineSegment(sketch, "E360", {"start": v(13.74, 9.84) * mm, "end": v(13.17, 10.7) * mm});
            skLineSegment(sketch, "E361", {"start": v(13.17, 10.7) * mm, "end": v(11.9, 11.8) * mm});
            skLineSegment(sketch, "E362", {"start": v(11.9, 11.8) * mm, "end": v(11.52, 11.99) * mm});
            skLineSegment(sketch, "E363", {"start": v(11.52, 11.99) * mm, "end": v(10.78, 11.76) * mm});
            skLineSegment(sketch, "E364", {"start": v(10.78, 11.76) * mm, "end": v(10.1, 11.4) * mm});
            skLineSegment(sketch, "E365", {"start": v(10.1, 11.4) * mm, "end": v(9.96, 11) * mm});
            skLineSegment(sketch, "E366", {"start": v(9.96, 11) * mm, "end": v(9.84, 9.32) * mm});
            skLineSegment(sketch, "E367", {"start": v(9.84, 9.32) * mm, "end": v(10.04, 8.3) * mm});
            skLineSegment(sketch, "E368", {"start": v(10.04, 8.3) * mm, "end": v(10.2, 7.98) * mm});
            skLineSegment(sketch, "E369", {"start": v(10.2, 7.98) * mm, "end": v(10.98, 7.1) * mm});
            skLineSegment(sketch, "E370", {"start": v(10.98, 7.1) * mm, "end": v(11.09, 6.17) * mm});
            skLineSegment(sketch, "E371", {"start": v(11.09, 6.17) * mm, "end": v(9.48, 4.56) * mm});
            skLineSegment(sketch, "E372", {"start": v(9.48, 4.56) * mm, "end": v(8.56, 4.67) * mm});
            skLineSegment(sketch, "E373", {"start": v(8.56, 4.67) * mm, "end": v(7.67, 5.45) * mm});
            skLineSegment(sketch, "E374", {"start": v(7.67, 5.45) * mm, "end": v(7.34, 5.6) * mm});
            skLineSegment(sketch, "E375", {"start": v(7.34, 5.6) * mm, "end": v(6.33, 5.8) * mm});
            skLineSegment(sketch, "E376", {"start": v(6.33, 5.8) * mm, "end": v(4.65, 5.7) * mm});
            skLineSegment(sketch, "E377", {"start": v(4.65, 5.7) * mm, "end": v(4.25, 5.56) * mm});
            skLineSegment(sketch, "E378", {"start": v(14.52, 1.65) * mm, "end": v(14.89, 1.85) * mm});
            skLineSegment(sketch, "E379", {"start": v(14.89, 1.85) * mm, "end": v(15.29, 1.97) * mm});
            skLineSegment(sketch, "E380", {"start": v(15.29, 1.97) * mm, "end": v(15.7, 2) * mm});
            skLineSegment(sketch, "E381", {"start": v(15.7, 2) * mm, "end": v(16.12, 1.94) * mm});
            skLineSegment(sketch, "E382", {"start": v(16.12, 1.94) * mm, "end": v(16.51, 1.8) * mm});
            skLineSegment(sketch, "E383", {"start": v(16.51, 1.8) * mm, "end": v(16.87, 1.59) * mm});
            skLineSegment(sketch, "E384", {"start": v(16.87, 1.59) * mm, "end": v(17.17, 1.3) * mm});
            skLineSegment(sketch, "E385", {"start": v(17.17, 1.3) * mm, "end": v(17.4, 0.95) * mm});
            skLineSegment(sketch, "E386", {"start": v(17.4, 0.95) * mm, "end": v(17.57, 0.57) * mm});
            skLineSegment(sketch, "E387", {"start": v(17.57, 0.57) * mm, "end": v(17.64, 0.16) * mm});
            skLineSegment(sketch, "E388", {"start": v(17.64, 0.16) * mm, "end": v(17.63, -0.26) * mm});
            skLineSegment(sketch, "E389", {"start": v(17.63, -0.26) * mm, "end": v(17.54, -0.67) * mm});
            skLineSegment(sketch, "E390", {"start": v(17.54, -0.67) * mm, "end": v(17.36, -1.04) * mm});
            skLineSegment(sketch, "E391", {"start": v(17.36, -1.04) * mm, "end": v(17.1, -1.38) * mm});
            skLineSegment(sketch, "E392", {"start": v(17.1, -1.38) * mm, "end": v(16.78, -1.65) * mm});
            skLineSegment(sketch, "E393", {"start": v(16.78, -1.65) * mm, "end": v(16.42, -1.85) * mm});
            skLineSegment(sketch, "E394", {"start": v(16.42, -1.85) * mm, "end": v(16.01, -1.97) * mm});
            skLineSegment(sketch, "E395", {"start": v(16.01, -1.97) * mm, "end": v(15.6, -2) * mm});
            skLineSegment(sketch, "E396", {"start": v(15.6, -2) * mm, "end": v(15.18, -1.94) * mm});
            skLineSegment(sketch, "E397", {"start": v(15.18, -1.94) * mm, "end": v(14.79, -1.8) * mm});
            skLineSegment(sketch, "E398", {"start": v(14.79, -1.8) * mm, "end": v(14.43, -1.59) * mm});
            skLineSegment(sketch, "E399", {"start": v(14.43, -1.59) * mm, "end": v(14.13, -1.3) * mm});
            skLineSegment(sketch, "E400", {"start": v(14.13, -1.3) * mm, "end": v(13.9, -0.95) * mm});
            skLineSegment(sketch, "E401", {"start": v(13.9, -0.95) * mm, "end": v(13.73, -0.57) * mm});
            skLineSegment(sketch, "E402", {"start": v(13.73, -0.57) * mm, "end": v(13.66, -0.16) * mm});
            skLineSegment(sketch, "E403", {"start": v(13.66, -0.16) * mm, "end": v(13.67, 0.26) * mm});
            skLineSegment(sketch, "E404", {"start": v(13.67, 0.26) * mm, "end": v(13.77, 0.67) * mm});
            skLineSegment(sketch, "E405", {"start": v(13.77, 0.67) * mm, "end": v(13.95, 1.04) * mm});
            skLineSegment(sketch, "E406", {"start": v(13.95, 1.04) * mm, "end": v(14.2, 1.38) * mm});
            skLineSegment(sketch, "E407", {"start": v(14.2, 1.38) * mm, "end": v(14.52, 1.65) * mm});
            skSolve(sketch);
        }
        {
            var Q0;
            Q0=makeQuery(id+"F0.imprint","IMPRINT",FACE,{"disambiguationData":[TD([[makeQuery(id+"F0.imprint","IMPRINT",EDGE,{"derivedFrom":sQuery(id+"F0.wireOp",EDGE,"E228")}),-1.0]])]});
            var sketch = newSketch(context, id + "F1", { "sketchPlane" : qUnion([Q0])});
            skPoint(sketch, "E408.0", {"position": v(-10.8, 1.72) * mm});
            skPoint(sketch, "E409.0", {"position": v(-10.43, 1.9) * mm});
            skPoint(sketch, "E410.0", {"position": v(-10.02, 1.98) * mm});
            skLineSegment(sketch, "E411", {"start": v(-10.8, 1.72) * mm, "end": v(-9.33, -0.84) * mm, "construction": true});
            skLineSegment(sketch, "E412", {"start": v(-10.43, 1.9) * mm, "end": v(-9.65, -0.51) * mm, "construction": true});
            skCircle(sketch, "E413", {"center": v(-9.81, 0) * mm, "radius": 3.5 * mm});
            skSolve(sketch);
        }
        {
            var Q0;
            Q0=makeQuery(id+"F0.imprint","IMPRINT",FACE,{"disambiguationData":[TD([[makeQuery(id+"F0.imprint","IMPRINT",EDGE,{"derivedFrom":sQuery(id+"F0.wireOp",EDGE,"E258")}),1.0]])]});
            var sketch = newSketch(context, id + "F2", { "sketchPlane" : qUnion([Q0])});
            skPoint(sketch, "E414.0", {"position": v(14.36, 1.51) * mm});
            skPoint(sketch, "E415.0", {"position": v(14.7, 1.75) * mm});
            skLineSegment(sketch, "E416", {"start": v(14.36, 1.51) * mm, "end": v(15.95, -0.36) * mm, "construction": true});
            skLineSegment(sketch, "E417", {"start": v(14.7, 1.75) * mm, "end": v(15.82, -0.3) * mm, "construction": true});
            skCircle(sketch, "E418", {"center": v(15.65, 0) * mm, "radius": 3 * mm});
            skSolve(sketch);
        }
        {
            var Q0;
            Q0=makeQuery(id+"F0.imprint","IMPRINT",FACE,{"disambiguationData":[TD([[makeQuery(id+"F0.imprint","IMPRINT",EDGE,{"derivedFrom":sQuery(id+"F0.wireOp",EDGE,"E0")}),1.0]])]});
            var Q1;
            Q1=makeQuery(id+"F0.imprint","IMPRINT",FACE,{"disambiguationData":[TD([[makeQuery(id+"F0.imprint","IMPRINT",EDGE,{"derivedFrom":sQuery(id+"F0.wireOp",EDGE,"E258")}),1.0]])]});
            extrude(context, id + "F3", {"entities" : qUnion([Q0, Q1]), "depth" : 15 * mm, "offsetDistance" : 25 * mm});
        }
        {
            var Q0;
            Q0=makeQuery(id+"F2.imprint","IMPRINT",FACE,{"disambiguationData":[TD([[makeQuery(id+"F2.imprint","IMPRINT",EDGE,{"derivedFrom":sQuery(id+"F2.wireOp",EDGE,"E418")}),1.0]])]});
            var Q1;
            Q1=makeQuery(id+"F1.imprint","IMPRINT",FACE,{"disambiguationData":[TD([[makeQuery(id+"F1.imprint","IMPRINT",EDGE,{"derivedFrom":sQuery(id+"F1.wireOp",EDGE,"E413")}),1.0]])]});
            extrude(context, id + "F4", {"entities" : qUnion([Q0, Q1]), "operationType" : NewBodyOperationType.REMOVE, "depth" : 25 * mm, "offsetDistance" : 25 * mm});
        }
    });
